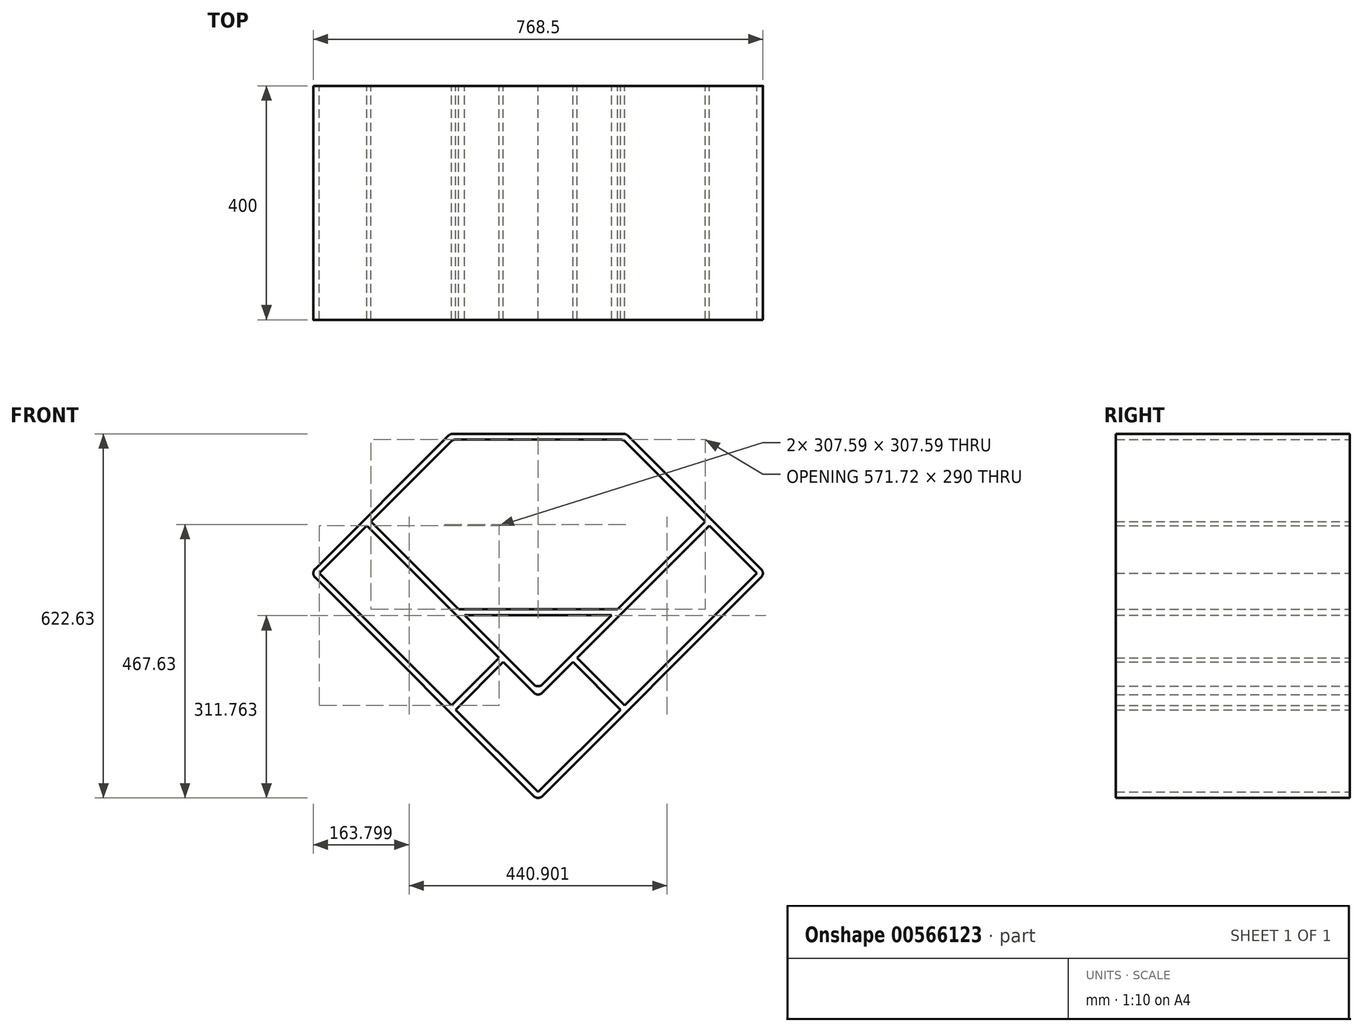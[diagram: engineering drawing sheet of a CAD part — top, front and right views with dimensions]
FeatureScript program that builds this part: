
annotation { "Feature Type Name" : "Feature", "Feature Type Description" : "" }
export const myFeature = defineFeature(function(context is Context, id is Id, definition is map)
    precondition{}
    {
        {
            var Q0;
            Q0=qCreatedBy(makeId("Front.planeOp"),FACE);
            var sketch = newSketch(context, id + "F0", { "sketchPlane" : qUnion([Q0])});
            skLineSegment(sketch, "E0", {"start": v(-300, 0) * mm, "end": v(-152.93, 147.07) * mm});
            skLineSegment(sketch, "E1", {"start": v(152.93, 147.07) * mm, "end": v(300, 0) * mm});
            skLineSegment(sketch, "E2", {"start": v(150, -150) * mm, "end": v(7.07, -292.93) * mm});
            skLineSegment(sketch, "E3", {"start": v(-7.07, -292.93) * mm, "end": v(-150, -150) * mm});
            skPoint(sketch, "E4.endSnap0", {"position": v(150, 150) * mm});
            skLineSegment(sketch, "E5.0", {"start": v(-7.07, -278.79) * mm, "end": v(-135.86, -150) * mm});
            skLineSegment(sketch, "E5.1", {"start": v(135.86, -150) * mm, "end": v(7.07, -278.79) * mm});
            skLineSegment(sketch, "E6", {"start": v(225, -75) * mm, "end": v(150, -150) * mm});
            skPoint(sketch, "E7.orphan", {"position": v(0, 300) * mm});
            skLineSegment(sketch, "E8", {"start": v(-145.86, 150) * mm, "end": v(145.86, 150) * mm});
            skLineSegment(sketch, "E9.1", {"start": v(-285.86, 0) * mm, "end": v(-148.79, 137.07) * mm});
            skLineSegment(sketch, "E9.3", {"start": v(-141.72, 140) * mm, "end": v(141.72, 140) * mm});
            skLineSegment(sketch, "E9.7", {"start": v(148.79, 137.07) * mm, "end": v(285.86, 0) * mm});
            skLineSegment(sketch, "E10", {"start": v(-300, 0) * mm, "end": v(-381.32, -81.32) * mm});
            skLineSegment(sketch, "E11", {"start": v(-381.32, -95.46) * mm, "end": v(-155.04, -321.73) * mm});
            skLineSegment(sketch, "E12", {"start": v(-140.9, -321.73) * mm, "end": v(-59.58, -240.42) * mm});
            skLineSegment(sketch, "E13.2", {"start": v(-374.25, -88.39) * mm, "end": v(-147.97, -314.66) * mm});
            skLineSegment(sketch, "E14", {"start": v(-300, 0) * mm, "end": v(-150, -150) * mm});
            skLineSegment(sketch, "E15", {"start": v(300, 0) * mm, "end": v(381.32, -81.32) * mm});
            skLineSegment(sketch, "E16", {"start": v(381.32, -95.46) * mm, "end": v(155.04, -321.73) * mm});
            skLineSegment(sketch, "E17", {"start": v(140.9, -321.73) * mm, "end": v(59.58, -240.42) * mm});
            skLineSegment(sketch, "E18.2", {"start": v(374.25, -88.39) * mm, "end": v(147.97, -314.66) * mm});
            skLineSegment(sketch, "E19", {"start": v(300, 0) * mm, "end": v(225, -75) * mm});
            skCircle(sketch, "E20", {"center": v(-150, 30) * mm, "radius": 65 * mm});
            skCircle(sketch, "E21", {"center": v(150, 30) * mm, "radius": 65 * mm});
            skPoint(sketch, "E22.end.orphan", {"position": v(-103.78, -284.61) * mm});
            skLineSegment(sketch, "E23", {"start": v(-135.86, -150) * mm, "end": v(135.86, -150) * mm});
            skLineSegment(sketch, "E24.0", {"start": v(-125.86, -160) * mm, "end": v(125.86, -160) * mm});
            skPoint(sketch, "E25.visualSharp", {"position": v(-388.39, -88.39) * mm});
            skArc(sketch, "E25.filletArc", {"start": v(-381.32, -81.32) * mm, "mid": v(-384.25, -88.39) * mm, "end": v(-381.32, -95.46) * mm});
            skPoint(sketch, "E26.visualSharp", {"position": v(-147.97, -328.8) * mm});
            skArc(sketch, "E26.filletArc", {"start": v(-155.04, -321.73) * mm, "mid": v(-147.97, -324.66) * mm, "end": v(-140.9, -321.73) * mm});
            skPoint(sketch, "E27.visualSharp", {"position": v(147.97, -328.8) * mm});
            skArc(sketch, "E27.filletArc", {"start": v(140.9, -321.73) * mm, "mid": v(147.97, -324.66) * mm, "end": v(155.04, -321.73) * mm});
            skPoint(sketch, "E28.visualSharp", {"position": v(388.39, -88.39) * mm});
            skArc(sketch, "E28.filletArc", {"start": v(381.32, -95.46) * mm, "mid": v(384.25, -88.39) * mm, "end": v(381.32, -81.32) * mm});
            skPoint(sketch, "E29.visualSharp", {"position": v(0, -300) * mm});
            skArc(sketch, "E29.filletArc", {"start": v(-7.07, -292.93) * mm, "mid": v(0, -295.86) * mm, "end": v(7.07, -292.93) * mm});
            skArc(sketch, "E30.filletArc", {"start": v(-7.07, -278.79) * mm, "mid": v(0, -281.72) * mm, "end": v(7.07, -278.79) * mm});
            skPoint(sketch, "E31.visualSharp", {"position": v(-150, 150) * mm});
            skArc(sketch, "E31.filletArc", {"start": v(-145.86, 150) * mm, "mid": v(-149.68, 149.24) * mm, "end": v(-152.93, 147.07) * mm});
            skArc(sketch, "E32.filletArc", {"start": v(-141.72, 140) * mm, "mid": v(-145.54, 139.24) * mm, "end": v(-148.79, 137.07) * mm});
            skPoint(sketch, "E33.visualSharp", {"position": v(145.86, 140) * mm});
            skArc(sketch, "E33.filletArc", {"start": v(148.79, 137.07) * mm, "mid": v(145.54, 139.24) * mm, "end": v(141.72, 140) * mm});
            skArc(sketch, "E34.filletArc", {"start": v(152.93, 147.07) * mm, "mid": v(149.68, 149.24) * mm, "end": v(145.86, 150) * mm});
            skLineSegment(sketch, "E35", {"start": v(-155.04, -321.73) * mm, "end": v(-7.07, -469.7) * mm});
            skLineSegment(sketch, "E36", {"start": v(7.07, -469.7) * mm, "end": v(155.04, -321.73) * mm});
            skLineSegment(sketch, "E37", {"start": v(-135.86, -150) * mm, "end": v(-285.86, 0) * mm});
            skLineSegment(sketch, "E38", {"start": v(285.86, 0) * mm, "end": v(135.86, -150) * mm});
            skPoint(sketch, "E39.visualSharp", {"position": v(0, -476.78) * mm});
            skArc(sketch, "E39.filletArc", {"start": v(-7.07, -469.7) * mm, "mid": v(0, -472.63) * mm, "end": v(7.07, -469.7) * mm});
            skLineSegment(sketch, "E40", {"start": v(-374.25, -88.39) * mm, "end": v(-292.93, -7.07) * mm});
            skLineSegment(sketch, "E41", {"start": v(-147.97, -314.66) * mm, "end": v(-66.65, -233.35) * mm});
            skLineSegment(sketch, "E42", {"start": v(374.25, -88.39) * mm, "end": v(292.93, -7.07) * mm});
            skLineSegment(sketch, "E43", {"start": v(147.97, -314.66) * mm, "end": v(66.65, -233.35) * mm});
            skLineSegment(sketch, "E44", {"start": v(-140.9, -321.73) * mm, "end": v(0, -462.63) * mm});
            skLineSegment(sketch, "E45", {"start": v(0, -462.63) * mm, "end": v(140.9, -321.73) * mm});
            skLineSegment(sketch, "E46", {"start": v(-210.86, -75) * mm, "end": v(210.86, -75) * mm});
            skLineSegment(sketch, "E47", {"start": v(-103.78, -284.61) * mm, "end": v(-107.31, -281.07) * mm});
            skPoint(sketch, "E47.endSnap0", {"position": v(-100.24, -281.07) * mm});
            skLineSegment(sketch, "E48", {"start": v(-292.93, 0) * mm, "end": v(-289.07, -3.86) * mm});
            skLineSegment(sketch, "E49", {"start": v(-292.93, 0) * mm, "end": v(0, -292.93) * mm});
            skSolve(sketch);
        }
        {
            var Q0;
            Q0=qSketchRegion(id+"F0",true);
            var Q1;
            {var subQ0=sQuery(id+"F0.wireOp",EDGE,"f3315127-8726-48a4-a6a5-5769ba37091d.0");Q1=makeQuery(id+"F0.imprint","IMPRINT",FACE,{"disambiguationData":[TD([[makeQuery(id+"F0.imprint","IMPRINT",EDGE,{"derivedFrom":subQ0}),-1.0]])]});}
            var Q2;
            {var subQ0=sQuery(id+"F0.wireOp",EDGE,"E23");Q2=makeQuery(id+"F0.imprint","IMPRINT",FACE,{"disambiguationData":[TD([[makeQuery(id+"F0.imprint","IMPRINT",EDGE,{"derivedFrom":subQ0}),-1.0]])]});}
            extrude(context, id + "F1", {"entities" : qUnion([Q0, Q1, Q2]), "depth" : 400 * mm, "offsetDistance" : 25 * mm});
        }
    });
